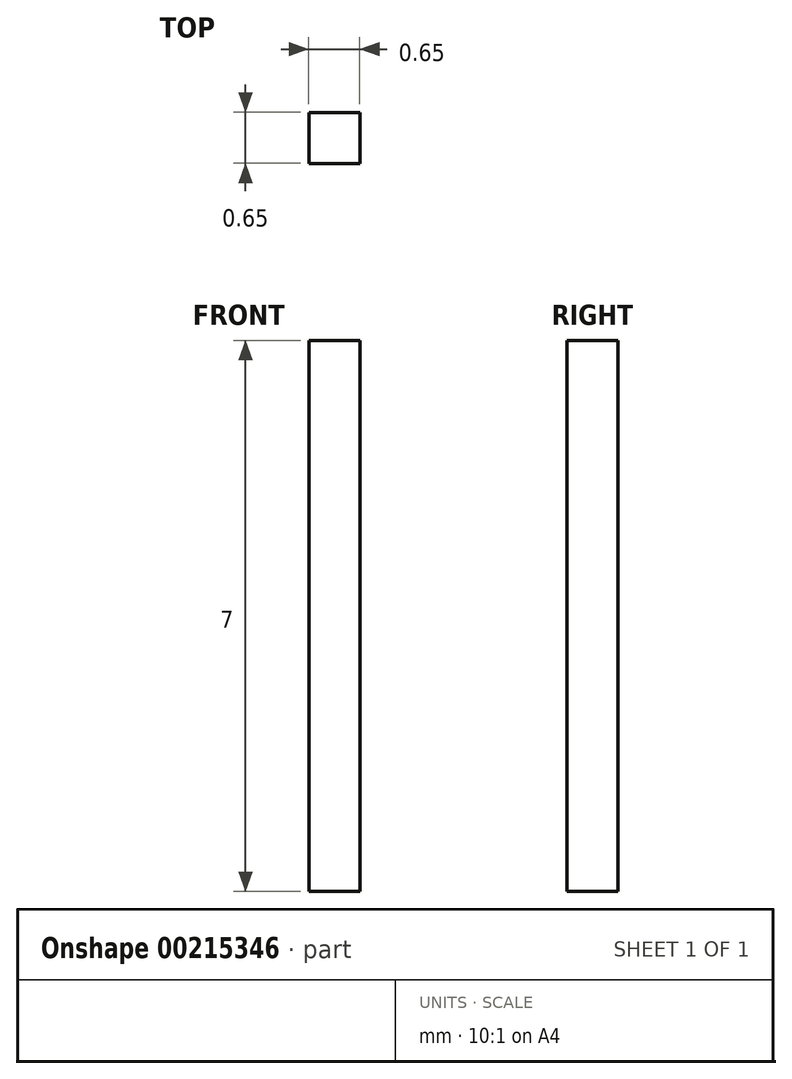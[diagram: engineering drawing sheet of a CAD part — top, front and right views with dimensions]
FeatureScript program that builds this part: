
annotation { "Feature Type Name" : "Feature", "Feature Type Description" : "" }
export const myFeature = defineFeature(function(context is Context, id is Id, definition is map)
    precondition{}
    {
        {
            var Q0;
            Q0=qCreatedBy(makeId("Top.planeOp"),FACE);
            var sketch = newSketch(context, id + "F0", { "sketchPlane" : qUnion([Q0])});
            skLineSegment(sketch, "E0.bottom", {"start": v(10.26, -12.53) * mm, "end": v(10.91, -12.53) * mm});
            skLineSegment(sketch, "E0.top", {"start": v(10.26, -13.18) * mm, "end": v(10.91, -13.18) * mm});
            skLineSegment(sketch, "E0.left", {"start": v(10.26, -12.53) * mm, "end": v(10.26, -13.18) * mm});
            skLineSegment(sketch, "E0.right", {"start": v(10.91, -12.53) * mm, "end": v(10.91, -13.18) * mm});
            skSolve(sketch);
        }
        {
            var Q0;
            Q0 = qSketchRegion(id + "F0", true);
            extrude(context, id + "F1", {"entities" : qUnion([Q0]), "depth" : 7 * mm});
        }
    });
